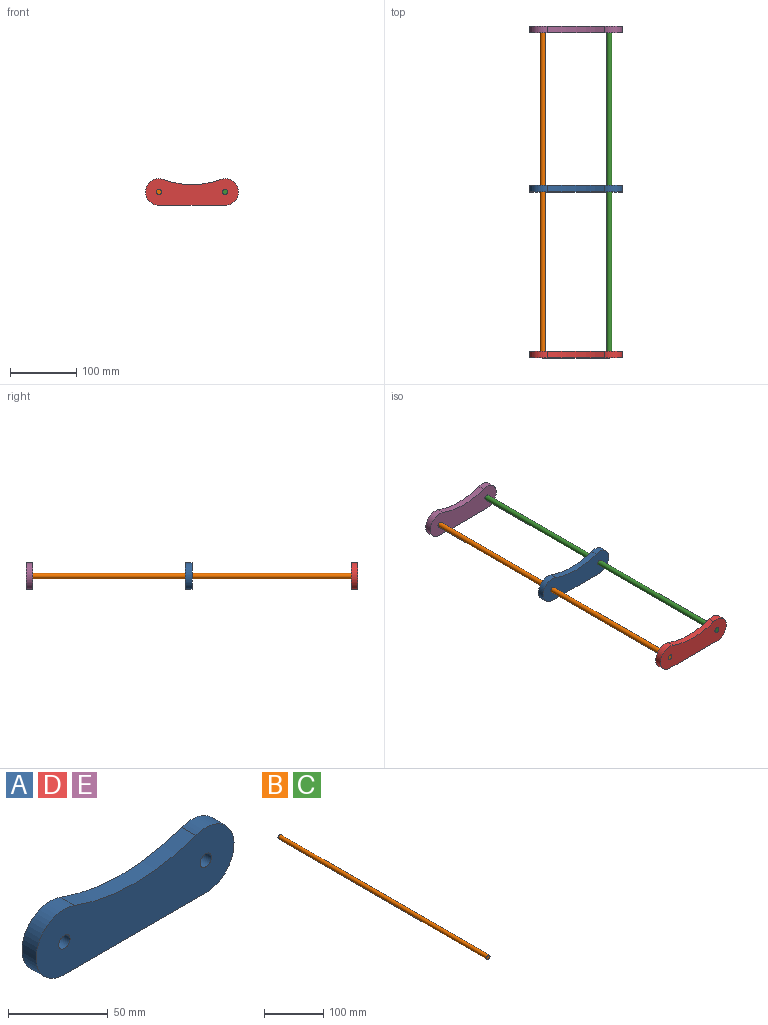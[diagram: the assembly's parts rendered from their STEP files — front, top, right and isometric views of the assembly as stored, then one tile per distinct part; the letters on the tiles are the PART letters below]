
ASSEMBLY  parts=5 mates=4
PART A: 8 faces, bbox 140x10x40 mm
  f0: cylinder r=122.73mm len=85.99mm, axis (0,1,0), area 878.5mm2, adj f1,f4,f6,f7
  f1: cylinder r=20mm len=40mm, axis (0,1,0), area 699.9mm2, adj f0,f2,f6,f7
  f2: plane 100x10mm, normal (0,0,-1), area 1000mm2, adj f1,f4,f6,f7
  f3: cylinder r=4mm len=10mm, axis (0,1,0), area 251.3mm2, adj f6,f7
  f4: cylinder r=20mm len=40mm, axis (0,1,0), area 699.9mm2, adj f0,f2,f6,f7
  f5: cylinder r=4mm len=10mm, axis (0,1,0), area 251.3mm2, adj f6,f7
  f6: plane 140x40mm, normal (0,-1,0), area 4592.6mm2, adj f0,f1,f2,f3,f4,f5
  f7: plane 140x40mm, normal (0,1,0), area 4592.6mm2, adj f0,f1,f2,f3,f4,f5
PART B: 3 faces, bbox 8x500x8 mm
  f0: cylinder r=4mm len=500mm, axis (0,1,0), area 12566.4mm2, adj f1,f2
  f1: plane 8x8mm, normal (0,-1,0), area 50.3mm2, adj f0
  f2: plane 8x8mm, normal (0,1,0), area 50.3mm2, adj f0
PART C: same geometry as B
PART D: same geometry as A
PART E: same geometry as A
PLACE A t=(-32.75,241.01,-9.53)mm
PLACE B t=(-90.55,231.01,10.47)mm
PLACE C t=(9.45,231.01,10.47)mm
PLACE D t=(-32.75,-8.99,-9.53)mm
PLACE E t=(-32.75,481.01,-9.53)mm
MATE cylindrical B.f0 <-> D.f1  axis (0,-1,0) through (-90.55,-18.99,10.47)mm
MATE cylindrical C.f0 <-> D.f4  axis (0,-1,0) through (9.45,-18.99,10.47)mm
MATE cylindrical A.f4 <-> C.f0  axis (0,-1,0) through (9.45,231.01,10.47)mm
MATE cylindrical E.f1 <-> B.f0  axis (0,1,0) through (-90.55,481.01,10.47)mm
